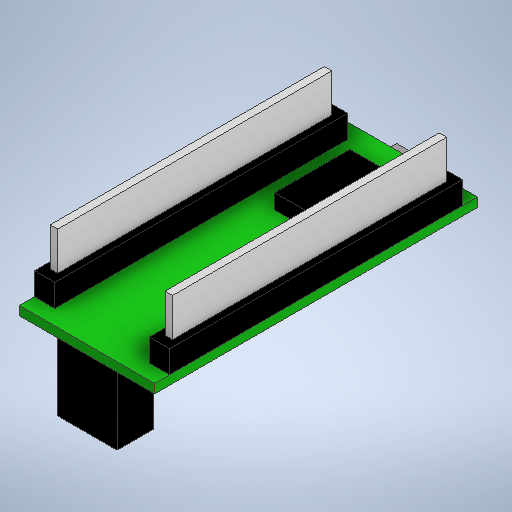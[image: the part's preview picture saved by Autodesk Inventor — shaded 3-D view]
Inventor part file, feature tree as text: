
AUTODESK INVENTOR PART (.ipt)
format: ipt  version: 2025.2 (Build 292293000, 293)  size: 316,416 bytes
history: native  units: mm
features: extrude x6, sketch x6
ambient origin geometry x8: Origin, YZ Plane, XZ Plane, XY Plane, X Axis, Y Axis, Z Axis, Center Point
bodies: Solid1 (feature_tree)
feature tree (12):
  extrude  "Extrusion1"  Depth=43.0mm
  extrude  "Extrusion2"  Depth=0.001mm
  extrude  "Extrusion3"  Depth=2.0mm
  extrude  "Extrusion4"  Depth=3.0mm TaperAngle=0.0deg
  extrude  "Extrusion5"  Depth=10.0mm
  extrude  "Extrusion6"  Depth=6.0mm
  sketch  "Sketch1"  dims[d0=18.0mm d1=43.0mm]
  sketch  "Sketch2"  dims[d2=1.2mm d3=0.0mm d4=0.001mm]
  sketch  "Sketch3"  dims[d5=2.0mm d6=2.0mm]
  sketch  "Sketch4"  dims[d7=2.7mm d8=3.0mm d9=0.0mm]
  sketch  "Sketch5"  dims[d10=5.0mm d11=10.0mm]
  sketch  "Sketch6"  dims[d12=6.0mm d13=6.0mm d14=2.0mm d15=0.0mm d16=7.0mm d17=5.25mm d18=5.75mm d19=7.0mm d20=2.0mm d21=4.0mm d22=0.0mm d23=5.0mm d24=5.0mm d25=0.001mm d26=4.9mm d27=9.0mm d28=0.0mm d29=1.0mm d30=36.5mm d31=0.85mm d32=0.85mm d33=1.25mm d34=1.25mm d35=5.1mm d36=0.0mm d37=0.5mm d38=0.872665mm]
